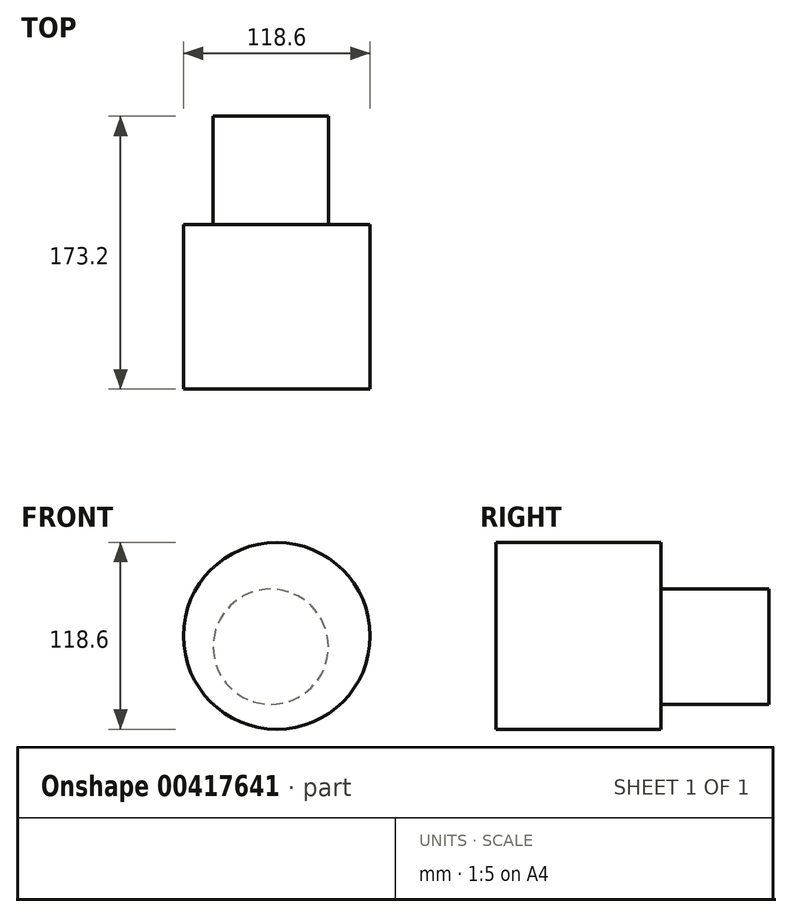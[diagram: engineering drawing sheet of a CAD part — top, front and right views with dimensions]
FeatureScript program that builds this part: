
annotation { "Feature Type Name" : "Feature", "Feature Type Description" : "" }
export const myFeature = defineFeature(function(context is Context, id is Id, definition is map)
    precondition{}
    {
        {
            var Q0;
            Q0=qCreatedBy(makeId("Front.planeOp"),FACE);
            var sketch = newSketch(context, id + "F0", { "sketchPlane" : qUnion([Q0])});
            skCircle(sketch, "E0", {"center": v(0, 0) * mm, "radius": 59.3 * mm});
            skCircle(sketch, "E1", {"center": v(0, 0) * mm, "radius": 45.14 * mm});
            skSolve(sketch);
        }
        {
            var Q0;
            Q0=makeQuery(id+"F0.imprint","IMPRINT",FACE,{"disambiguationData":[TD([[makeQuery(id+"F0.imprint","IMPRINT",EDGE,{"derivedFrom":sQuery(id+"F0.wireOp",EDGE,"E1")}),1.0]])]});
            var Q1;
            Q1=makeQuery(id+"F0.imprint","IMPRINT",FACE,{"disambiguationData":[TD([[makeQuery(id+"F0.imprint","IMPRINT",EDGE,{"derivedFrom":sQuery(id+"F0.wireOp",EDGE,"E0")}),1.0]])]});
            extrude(context, id + "F1", {"entities" : qUnion([Q0, Q1]), "depth" : 104.6 * mm});
        }
        {
            var Q0;
            Q0=makeQuery(id+"F1.opExtrude","CAP_FACE",FACE,{"disambiguationData":[OSD([sQuery(id+"F0.wireOp",EDGE,"E0")])],"isStart":false});
            var sketch = newSketch(context, id + "F2", { "sketchPlane" : qUnion([Q0])});
            skCircle(sketch, "E2", {"center": v(-3.86, -6.92) * mm, "radius": 36.57 * mm});
            skSolve(sketch);
        }
        {
            var Q0;
            Q0=makeQuery(id+"F2.imprint","IMPRINT",FACE,{"disambiguationData":[TD([[makeQuery(id+"F2.imprint","IMPRINT",EDGE,{"derivedFrom":sQuery(id+"F2.wireOp",EDGE,"E2")}),1.0]])]});
            extrude(context, id + "F3", {"entities" : qUnion([Q0]), "operationType" : NewBodyOperationType.ADD, "oppositeDirection" : true, "depth" : 173.2 * mm});
        }
    });
